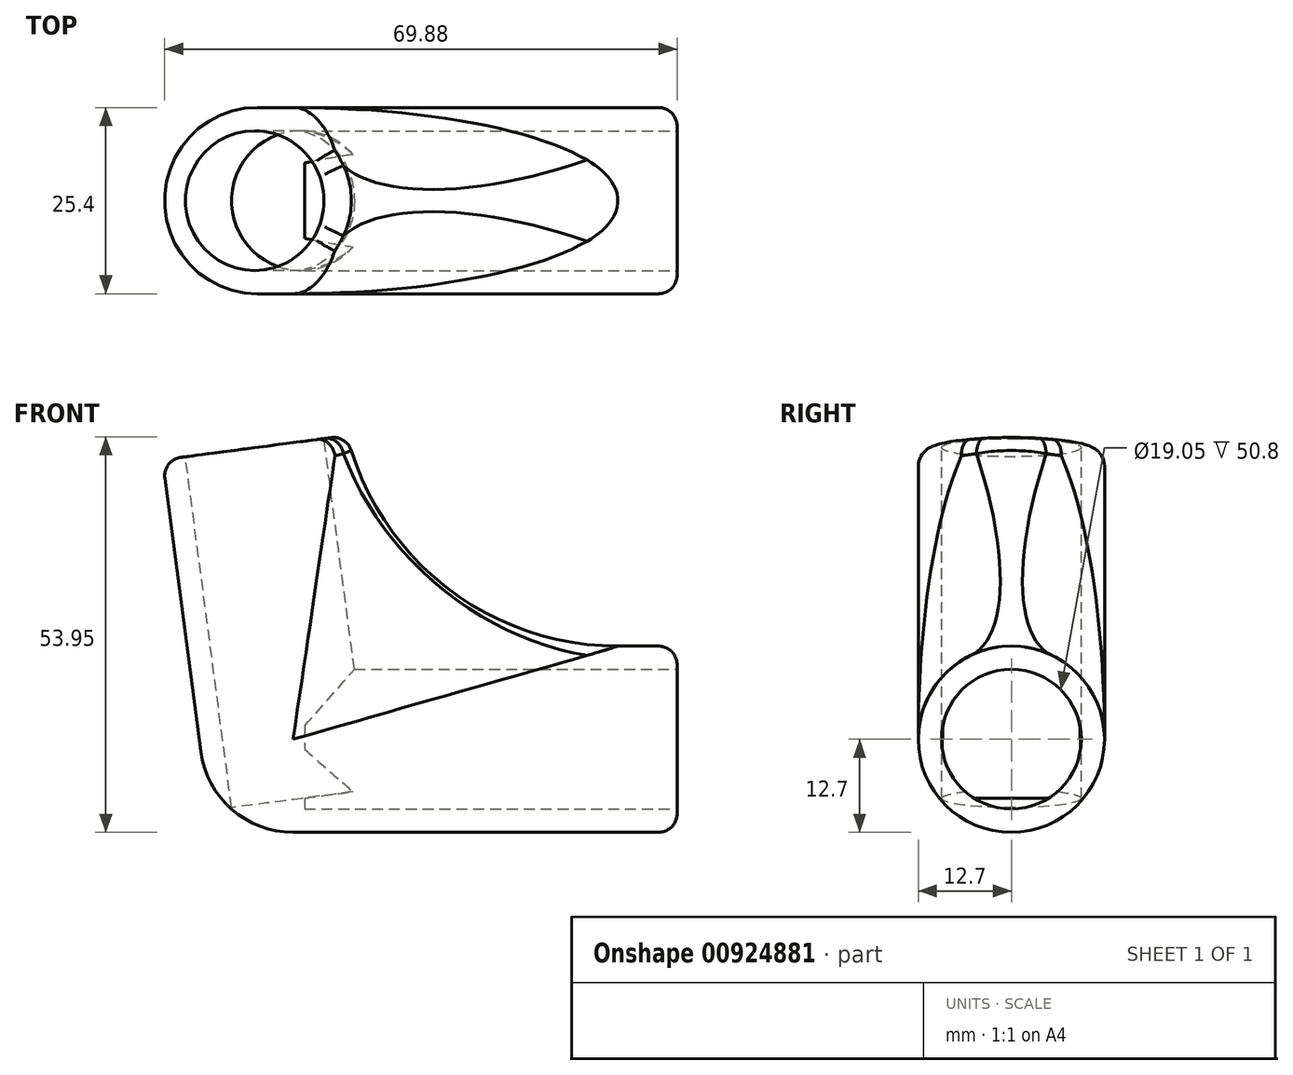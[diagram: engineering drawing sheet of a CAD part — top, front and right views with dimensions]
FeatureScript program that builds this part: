
annotation { "Feature Type Name" : "Feature", "Feature Type Description" : "" }
export const myFeature = defineFeature(function(context is Context, id is Id, definition is map)
    precondition{}
    {
        {
            var Q0;
            Q0=qCreatedBy(makeId("Front.planeOp"),FACE);
            var sketch = newSketch(context, id + "F0", { "sketchPlane" : qUnion([Q0])});
            skLineSegment(sketch, "E0.top", {"start": v(-45.74, -12.7) * mm, "end": v(17.76, -12.7) * mm});
            skLineSegment(sketch, "E0.right", {"start": v(17.76, 12.7) * mm, "end": v(17.76, -12.7) * mm});
            skLineSegment(sketch, "E1", {"start": v(-49.09, 12.7) * mm, "end": v(-52.43, 38.1) * mm});
            skLineSegment(sketch, "E2", {"start": v(-52.43, 38.1) * mm, "end": v(-27.25, 41.42) * mm});
            skLineSegment(sketch, "E3", {"start": v(-27.25, 41.42) * mm, "end": v(-23.47, 12.7) * mm});
            skLineSegment(sketch, "E4", {"start": v(-49.09, 12.7) * mm, "end": v(-45.74, -12.7) * mm});
            skLineSegment(sketch, "E5", {"start": v(17.76, 12.7) * mm, "end": v(-23.47, 12.7) * mm});
            skSolve(sketch);
        }
        {
            var Q0;
            Q0=qSketchRegion(id+"F0",true);
            extrude(context, id + "F1", {"entities" : qUnion([Q0]), "depth" : 25.4 * mm, "offsetDistance" : 25.4 * mm});
        }
        {
            var Q0;
            Q0=makeQuery(id+"F1.opExtrude","CAP_EDGE",EDGE,{"disambiguationData":[OSD([sQuery(id+"F0.wireOp",EDGE,"E0.left"),sQuery(id+"F0.wireOp",EDGE,"0F3Pt2aK-DOpA-Pfff-sn91-FgOYTT9K1tDF.left")])],"isStart":false});
            var Q1;
            Q1=makeQuery(id+"F1.opExtrude","CAP_EDGE",EDGE,{"disambiguationData":[OSD([sQuery(id+"F0.wireOp",EDGE,"0F3Pt2aK-DOpA-Pfff-sn91-FgOYTT9K1tDF.right")])],"isStart":false});
            var Q2;
            Q2=makeQuery(id+"F1.opExtrude","CAP_EDGE",EDGE,{"disambiguationData":[OSD([sQuery(id+"F0.wireOp",EDGE,"0F3Pt2aK-DOpA-Pfff-sn91-FgOYTT9K1tDF.right")])],"isStart":true});
            var Q3;
            Q3=makeQuery(id+"F1.opExtrude","CAP_EDGE",EDGE,{"disambiguationData":[OSD([sQuery(id+"F0.wireOp",EDGE,"E0.bottom")])],"isStart":false});
            var Q4;
            Q4=makeQuery(id+"F1.opExtrude","CAP_EDGE",EDGE,{"disambiguationData":[OSD([sQuery(id+"F0.wireOp",EDGE,"E0.top")])],"isStart":false});
            var Q5;
            Q5=makeQuery(id+"F1.opExtrude","CAP_EDGE",EDGE,{"disambiguationData":[OSD([sQuery(id+"F0.wireOp",EDGE,"E0.left"),sQuery(id+"F0.wireOp",EDGE,"0F3Pt2aK-DOpA-Pfff-sn91-FgOYTT9K1tDF.left")])],"isStart":true});
            var Q6;
            Q6=makeQuery(id+"F1.opExtrude","CAP_EDGE",EDGE,{"disambiguationData":[OSD([sQuery(id+"F0.wireOp",EDGE,"E0.bottom")])],"isStart":true});
            var Q7;
            Q7=makeQuery(id+"F1.opExtrude","CAP_EDGE",EDGE,{"disambiguationData":[OSD([sQuery(id+"F0.wireOp",EDGE,"E0.top")])],"isStart":true});
            var Q8;
            Q8=makeQuery(id+"F1.opExtrude","CAP_EDGE",EDGE,{"disambiguationData":[OSD([sQuery(id+"F0.wireOp",EDGE,"E1"),sQuery(id+"F0.wireOp",EDGE,"E4")])],"isStart":false});
            var Q9;
            Q9=makeQuery(id+"F1.opExtrude","CAP_EDGE",EDGE,{"disambiguationData":[OSD([sQuery(id+"F0.wireOp",EDGE,"E3")])],"isStart":false});
            var Q10;
            Q10=makeQuery(id+"F1.opExtrude","CAP_EDGE",EDGE,{"disambiguationData":[OSD([sQuery(id+"F0.wireOp",EDGE,"E5")])],"isStart":false});
            var Q11;
            Q11=makeQuery(id+"F1.opExtrude","CAP_EDGE",EDGE,{"disambiguationData":[OSD([sQuery(id+"F0.wireOp",EDGE,"E5")])],"isStart":true});
            var Q12;
            Q12=makeQuery(id+"F1.opExtrude","CAP_EDGE",EDGE,{"disambiguationData":[OSD([sQuery(id+"F0.wireOp",EDGE,"E3")])],"isStart":true});
            var Q13;
            Q13=makeQuery(id+"F1.opExtrude","CAP_EDGE",EDGE,{"disambiguationData":[OSD([sQuery(id+"F0.wireOp",EDGE,"E1"),sQuery(id+"F0.wireOp",EDGE,"E4")])],"isStart":true});
            var Q14;
            Q14=makeQuery(id+"F1.opExtrude","SWEPT_EDGE",EDGE,{"disambiguationData":[OSD([sQuery(id+"F0.wireOp",EDGE,"E0.top"),sQuery(id+"F0.wireOp",EDGE,"E4")])]});
            fillet(context, id + "F2", {"entities" : qUnion([Q0, Q1, Q2, Q3, Q4, Q5, Q6, Q7, Q8, Q9, Q10, Q11, Q12, Q13, Q14]), "radius" : 12.7 * mm, "tangentPropagation" : true, "allowEdgeOverflow" : false});
        }
        {
            var Q0;
            Q0=makeQuery(id+"F1.opExtrude","SWEPT_FACE",FACE,{"disambiguationData":[OSD([sQuery(id+"F0.wireOp",EDGE,"E0.right")])]});
            var sketch = newSketch(context, id + "F3", { "sketchPlane" : qUnion([Q0])});
            skCircle(sketch, "E6", {"center": v(-12.7, 0) * mm, "radius": 9.53 * mm});
            skSolve(sketch);
        }
        {
            var Q0;
            Q0=makeQuery(id+"F2.opFillet","BLEND_EDGE",EDGE,{"blendedFrom":[makeQuery(id+"F1.opExtrude","CAP_EDGE",EDGE,{"disambiguationData":[OSD([sQuery(id+"F0.wireOp",EDGE,"E3")])],"isStart":true}),makeQuery(id+"F1.opExtrude","CAP_EDGE",EDGE,{"disambiguationData":[OSD([sQuery(id+"F0.wireOp",EDGE,"E5")])],"isStart":true})],"blendedInto":[]});
            fillet(context, id + "F4", {"entities" : qUnion([Q0]), "radius" : 38.1 * mm, "tangentPropagation" : true, "allowEdgeOverflow" : false});
        }
        {
            var Q0;
            Q0=makeQuery(id+"F3.imprint","IMPRINT",FACE,{"disambiguationData":[TD([[makeQuery(id+"F3.imprint","IMPRINT",EDGE,{"derivedFrom":sQuery(id+"F3.wireOp",EDGE,"E6")}),1.0]])]});
            extrude(context, id + "F5", {"entities" : qUnion([Q0]), "operationType" : NewBodyOperationType.REMOVE, "oppositeDirection" : true, "depth" : 50.8 * mm, "offsetDistance" : 25.4 * mm});
        }
        {
            var Q0;
            Q0=makeQuery(id+"F1.opExtrude","SWEPT_FACE",FACE,{"disambiguationData":[OSD([sQuery(id+"F0.wireOp",EDGE,"E2")])]});
            var sketch = newSketch(context, id + "F6", { "sketchPlane" : qUnion([Q0])});
            skCircle(sketch, "E7", {"center": v(-34.31, -12.7) * mm, "radius": 9.53 * mm});
            skSolve(sketch);
        }
        {
            var Q0;
            Q0=makeQuery(id+"F6.imprint","IMPRINT",FACE,{"disambiguationData":[TD([[makeQuery(id+"F6.imprint","IMPRINT",EDGE,{"derivedFrom":sQuery(id+"F6.wireOp",EDGE,"E7")}),1.0]])]});
            extrude(context, id + "F7", {"entities" : qUnion([Q0]), "operationType" : NewBodyOperationType.REMOVE, "oppositeDirection" : true, "depth" : 48.26 * mm, "offsetDistance" : 25.4 * mm});
        }
        {
            var Q0;
            Q0=makeQuery(id+"F2.opFillet","BLEND_EDGE",EDGE,{"blendedFrom":[makeQuery(id+"F1.opExtrude","CAP_EDGE",EDGE,{"disambiguationData":[OSD([sQuery(id+"F0.wireOp",EDGE,"E0.top")])],"isStart":true}),makeQuery(id+"F1.opExtrude","SWEPT_FACE",FACE,{"disambiguationData":[OSD([sQuery(id+"F0.wireOp",EDGE,"E0.right")])]})],"blendedInto":[makeQuery(id+"F1.opExtrude","SWEPT_FACE",FACE,{"disambiguationData":[OSD([sQuery(id+"F0.wireOp",EDGE,"E0.right")])]})]});
            var Q1;
            Q1=makeQuery(id+"F2.opFillet","BLEND_EDGE",EDGE,{"blendedFrom":[makeQuery(id+"F1.opExtrude","CAP_EDGE",EDGE,{"disambiguationData":[OSD([sQuery(id+"F0.wireOp",EDGE,"E1"),sQuery(id+"F0.wireOp",EDGE,"E4")])],"isStart":true}),makeQuery(id+"F1.opExtrude","SWEPT_FACE",FACE,{"disambiguationData":[OSD([sQuery(id+"F0.wireOp",EDGE,"E2")])]})],"blendedInto":[makeQuery(id+"F1.opExtrude","SWEPT_FACE",FACE,{"disambiguationData":[OSD([sQuery(id+"F0.wireOp",EDGE,"E2")])]})]});
            fillet(context, id + "F8", {"entities" : qUnion([Q0, Q1]), "radius" : 2.54 * mm, "tangentPropagation" : true, "allowEdgeOverflow" : false});
        }
    });
